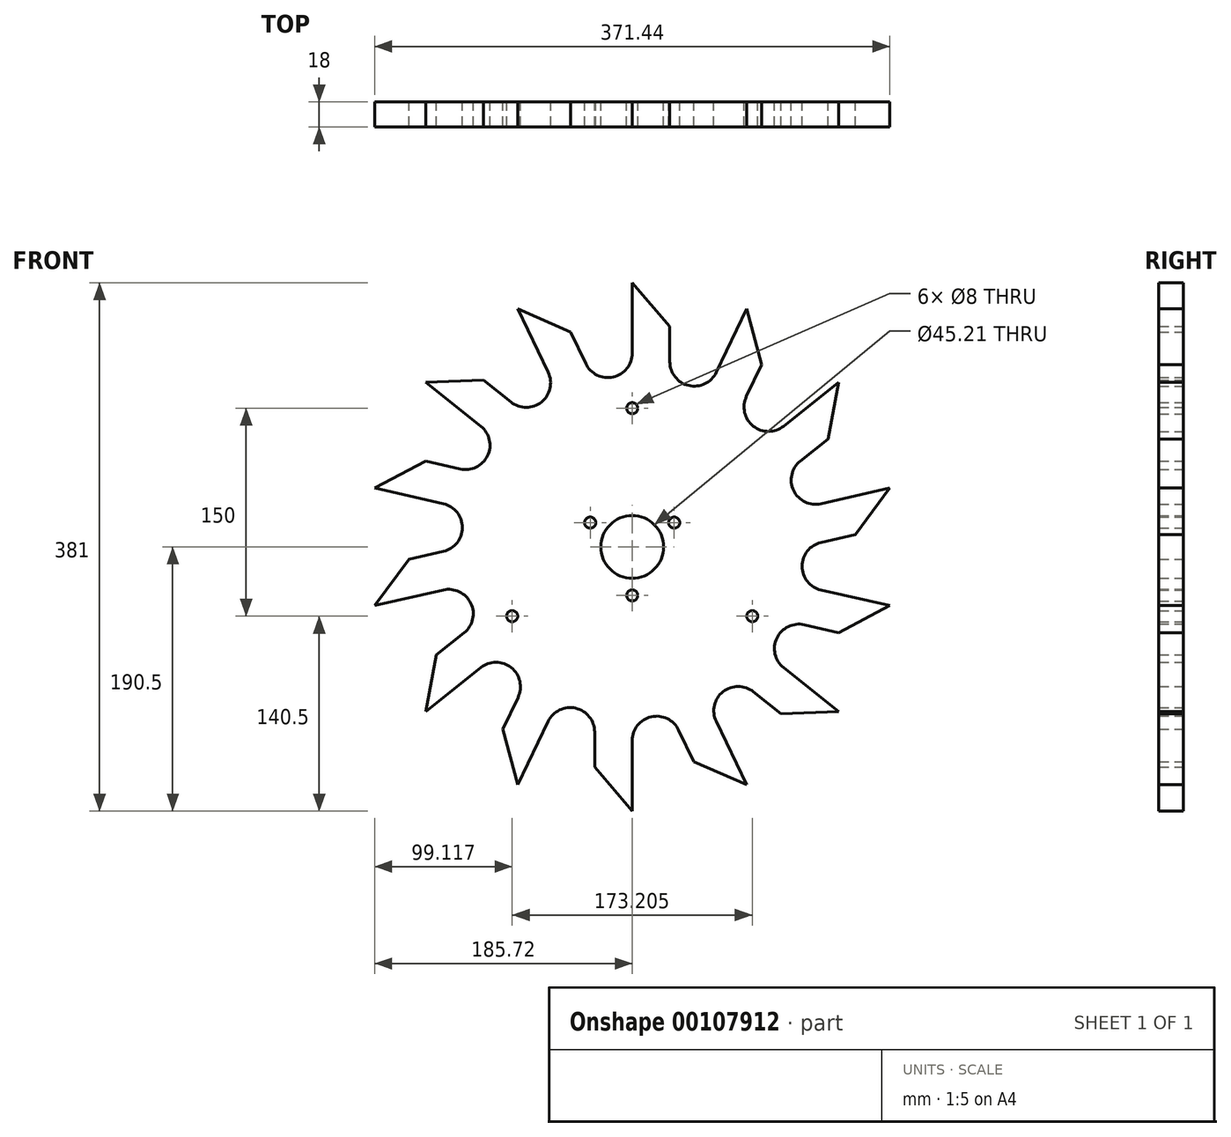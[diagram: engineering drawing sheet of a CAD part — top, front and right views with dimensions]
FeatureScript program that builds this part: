
annotation { "Feature Type Name" : "Feature", "Feature Type Description" : "" }
export const myFeature = defineFeature(function(context is Context, id is Id, definition is map)
    precondition{}
    {
        {
            var Q0;
            Q0=qCreatedBy(makeId("Front.planeOp"),FACE);
            var sketch = newSketch(context, id + "F0", { "sketchPlane" : qUnion([Q0])});
            skLineSegment(sketch, "E0", {"start": v(27.14, 158.9) * mm, "end": v(0, 190.5) * mm});
            skLineSegment(sketch, "E1", {"start": v(27.14, 158.9) * mm, "end": v(27.14, 133.5) * mm});
            skArc(sketch, "E2", {"start": v(27.14, 133.5) * mm, "mid": v(40.83, 116.34) * mm, "end": v(60.61, 125.87) * mm});
            skLineSegment(sketch, "E3", {"start": v(0, 190.5) * mm, "end": v(0, 139.7) * mm});
            skArc(sketch, "E4.1.0", {"start": v(-33.47, 132.06) * mm, "mid": v(-13.69, 122.53) * mm, "end": v(0, 139.7) * mm});
            skLineSegment(sketch, "E4.1.1", {"start": v(-82.65, 171.63) * mm, "end": v(-60.61, 125.87) * mm});
            skLineSegment(sketch, "E4.1.2", {"start": v(-44.5, 154.95) * mm, "end": v(-33.47, 132.06) * mm});
            skLineSegment(sketch, "E4.1.3", {"start": v(-44.5, 154.95) * mm, "end": v(-82.65, 171.63) * mm});
            skArc(sketch, "E4.2.0", {"start": v(-87.46, 104.46) * mm, "mid": v(-65.5, 104.46) * mm, "end": v(-60.61, 125.87) * mm});
            skLineSegment(sketch, "E4.2.1", {"start": v(-148.94, 118.77) * mm, "end": v(-109.22, 87.1) * mm});
            skLineSegment(sketch, "E4.2.2", {"start": v(-107.31, 120.3) * mm, "end": v(-87.46, 104.46) * mm});
            skLineSegment(sketch, "E4.2.3", {"start": v(-107.31, 120.3) * mm, "end": v(-148.94, 118.77) * mm});
            skLineSegment(sketch, "E5.4.3.0", {"start": v(-185.72, 42.4) * mm, "end": v(-136.2, 31.09) * mm});
            skArc(sketch, "E5.6.3.0", {"start": v(-124.12, 56.17) * mm, "mid": v(-104.34, 65.7) * mm, "end": v(-109.22, 87.1) * mm});
            skLineSegment(sketch, "E5.7.3.0", {"start": v(-148.88, 61.82) * mm, "end": v(-124.12, 56.17) * mm});
            skLineSegment(sketch, "E5.10.3.0", {"start": v(-148.88, 61.82) * mm, "end": v(-185.72, 42.4) * mm});
            skLineSegment(sketch, "E5.4.4.0", {"start": v(-185.72, -42.4) * mm, "end": v(-136.2, -31.09) * mm});
            skArc(sketch, "E5.6.4.0", {"start": v(-136.2, -3.25) * mm, "mid": v(-122.5, 13.92) * mm, "end": v(-136.2, 31.09) * mm});
            skLineSegment(sketch, "E5.7.4.0", {"start": v(-160.96, -8.9) * mm, "end": v(-136.2, -3.25) * mm});
            skLineSegment(sketch, "E5.10.4.0", {"start": v(-160.96, -8.9) * mm, "end": v(-185.72, -42.4) * mm});
            skLineSegment(sketch, "E5.4.5.0", {"start": v(-148.94, -118.77) * mm, "end": v(-109.22, -87.1) * mm});
            skArc(sketch, "E5.6.5.0", {"start": v(-121.3, -62.02) * mm, "mid": v(-116.42, -40.61) * mm, "end": v(-136.2, -31.09) * mm});
            skLineSegment(sketch, "E5.7.5.0", {"start": v(-141.16, -77.85) * mm, "end": v(-121.3, -62.02) * mm});
            skLineSegment(sketch, "E5.10.5.0", {"start": v(-141.16, -77.85) * mm, "end": v(-148.94, -118.77) * mm});
            skLineSegment(sketch, "E5.4.6.0", {"start": v(-82.65, -171.63) * mm, "end": v(-60.61, -125.87) * mm});
            skArc(sketch, "E5.6.6.0", {"start": v(-82.38, -108.5) * mm, "mid": v(-87.27, -87.1) * mm, "end": v(-109.22, -87.1) * mm});
            skLineSegment(sketch, "E5.7.6.0", {"start": v(-93.4, -131.4) * mm, "end": v(-82.38, -108.5) * mm});
            skLineSegment(sketch, "E5.10.6.0", {"start": v(-93.4, -131.4) * mm, "end": v(-82.65, -171.63) * mm});
            skLineSegment(sketch, "E5.4.7.0", {"start": v(0, -190.5) * mm, "end": v(0, -139.7) * mm});
            skArc(sketch, "E5.6.7.0", {"start": v(-27.14, -133.5) * mm, "mid": v(-40.83, -116.34) * mm, "end": v(-60.61, -125.87) * mm});
            skLineSegment(sketch, "E5.7.7.0", {"start": v(-27.14, -158.9) * mm, "end": v(-27.14, -133.5) * mm});
            skLineSegment(sketch, "E5.10.7.0", {"start": v(-27.14, -158.9) * mm, "end": v(0, -190.5) * mm});
            skLineSegment(sketch, "E5.4.8.0", {"start": v(82.65, -171.63) * mm, "end": v(60.61, -125.87) * mm});
            skArc(sketch, "E5.6.8.0", {"start": v(33.47, -132.06) * mm, "mid": v(13.69, -122.53) * mm, "end": v(0, -139.7) * mm});
            skLineSegment(sketch, "E5.7.8.0", {"start": v(44.5, -154.95) * mm, "end": v(33.47, -132.06) * mm});
            skLineSegment(sketch, "E5.10.8.0", {"start": v(44.5, -154.95) * mm, "end": v(82.65, -171.63) * mm});
            skLineSegment(sketch, "E5.4.9.0", {"start": v(148.94, -118.77) * mm, "end": v(109.22, -87.1) * mm});
            skArc(sketch, "E5.6.9.0", {"start": v(87.46, -104.46) * mm, "mid": v(65.5, -104.46) * mm, "end": v(60.61, -125.87) * mm});
            skLineSegment(sketch, "E5.7.9.0", {"start": v(107.31, -120.3) * mm, "end": v(87.46, -104.46) * mm});
            skLineSegment(sketch, "E5.10.9.0", {"start": v(107.31, -120.3) * mm, "end": v(148.94, -118.77) * mm});
            skLineSegment(sketch, "E5.4.10.0", {"start": v(185.72, -42.4) * mm, "end": v(136.2, -31.09) * mm});
            skArc(sketch, "E5.6.10.0", {"start": v(124.12, -56.17) * mm, "mid": v(104.34, -65.7) * mm, "end": v(109.22, -87.1) * mm});
            skLineSegment(sketch, "E5.7.10.0", {"start": v(148.88, -61.82) * mm, "end": v(124.12, -56.17) * mm});
            skLineSegment(sketch, "E5.10.10.0", {"start": v(148.88, -61.82) * mm, "end": v(185.72, -42.4) * mm});
            skLineSegment(sketch, "E5.4.11.0", {"start": v(185.72, 42.4) * mm, "end": v(136.2, 31.09) * mm});
            skArc(sketch, "E5.6.11.0", {"start": v(136.2, 3.25) * mm, "mid": v(122.5, -13.92) * mm, "end": v(136.2, -31.09) * mm});
            skLineSegment(sketch, "E5.7.11.0", {"start": v(160.96, 8.9) * mm, "end": v(136.2, 3.25) * mm});
            skLineSegment(sketch, "E5.10.11.0", {"start": v(160.96, 8.9) * mm, "end": v(185.72, 42.4) * mm});
            skLineSegment(sketch, "E5.4.12.0", {"start": v(148.94, 118.77) * mm, "end": v(109.22, 87.1) * mm});
            skArc(sketch, "E5.6.12.0", {"start": v(121.3, 62.02) * mm, "mid": v(116.42, 40.61) * mm, "end": v(136.2, 31.09) * mm});
            skLineSegment(sketch, "E5.7.12.0", {"start": v(141.16, 77.85) * mm, "end": v(121.3, 62.02) * mm});
            skLineSegment(sketch, "E5.10.12.0", {"start": v(141.16, 77.85) * mm, "end": v(148.94, 118.77) * mm});
            skLineSegment(sketch, "E5.4.13.0", {"start": v(82.65, 171.63) * mm, "end": v(60.61, 125.87) * mm});
            skArc(sketch, "E5.6.13.0", {"start": v(82.38, 108.5) * mm, "mid": v(87.27, 87.1) * mm, "end": v(109.22, 87.1) * mm});
            skLineSegment(sketch, "E5.7.13.0", {"start": v(93.4, 131.4) * mm, "end": v(82.38, 108.5) * mm});
            skLineSegment(sketch, "E5.10.13.0", {"start": v(93.4, 131.4) * mm, "end": v(82.65, 171.63) * mm});
            skLineSegment(sketch, "E6", {"start": v(0, 0) * mm, "end": v(0, 139.7) * mm, "construction": true});
            skCircle(sketch, "E7", {"center": v(0, 100) * mm, "radius": 4 * mm});
            skCircle(sketch, "E8.1.0", {"center": v(86.6, -50) * mm, "radius": 4 * mm});
            skCircle(sketch, "E8.2.0", {"center": v(-86.6, -50) * mm, "radius": 4 * mm});
            skLineSegment(sketch, "E8.anchor1", {"start": v(0, 0) * mm, "end": v(0, 100) * mm, "construction": true});
            skLineSegment(sketch, "E8.anchor2", {"start": v(0, 0) * mm, "end": v(-86.6, -50) * mm, "construction": true});
            skCircle(sketch, "E9", {"center": v(0, 0) * mm, "radius": 22.6 * mm});
            skCircle(sketch, "E10", {"center": v(0, -35) * mm, "radius": 4 * mm});
            skCircle(sketch, "E11.1.0", {"center": v(30.31, 17.5) * mm, "radius": 4 * mm});
            skCircle(sketch, "E11.2.0", {"center": v(-30.31, 17.5) * mm, "radius": 4 * mm});
            skCircle(sketch, "E12", {"center": v(0, 0) * mm, "radius": 150 * mm, "construction": true});
            skSolve(sketch);
        }
        {
            var Q0;
            Q0 = qSketchRegion(id + "F0", true);
            extrude(context, id + "F1", {"entities" : qUnion([Q0]), "depth" : 18 * mm});
        }
    });
